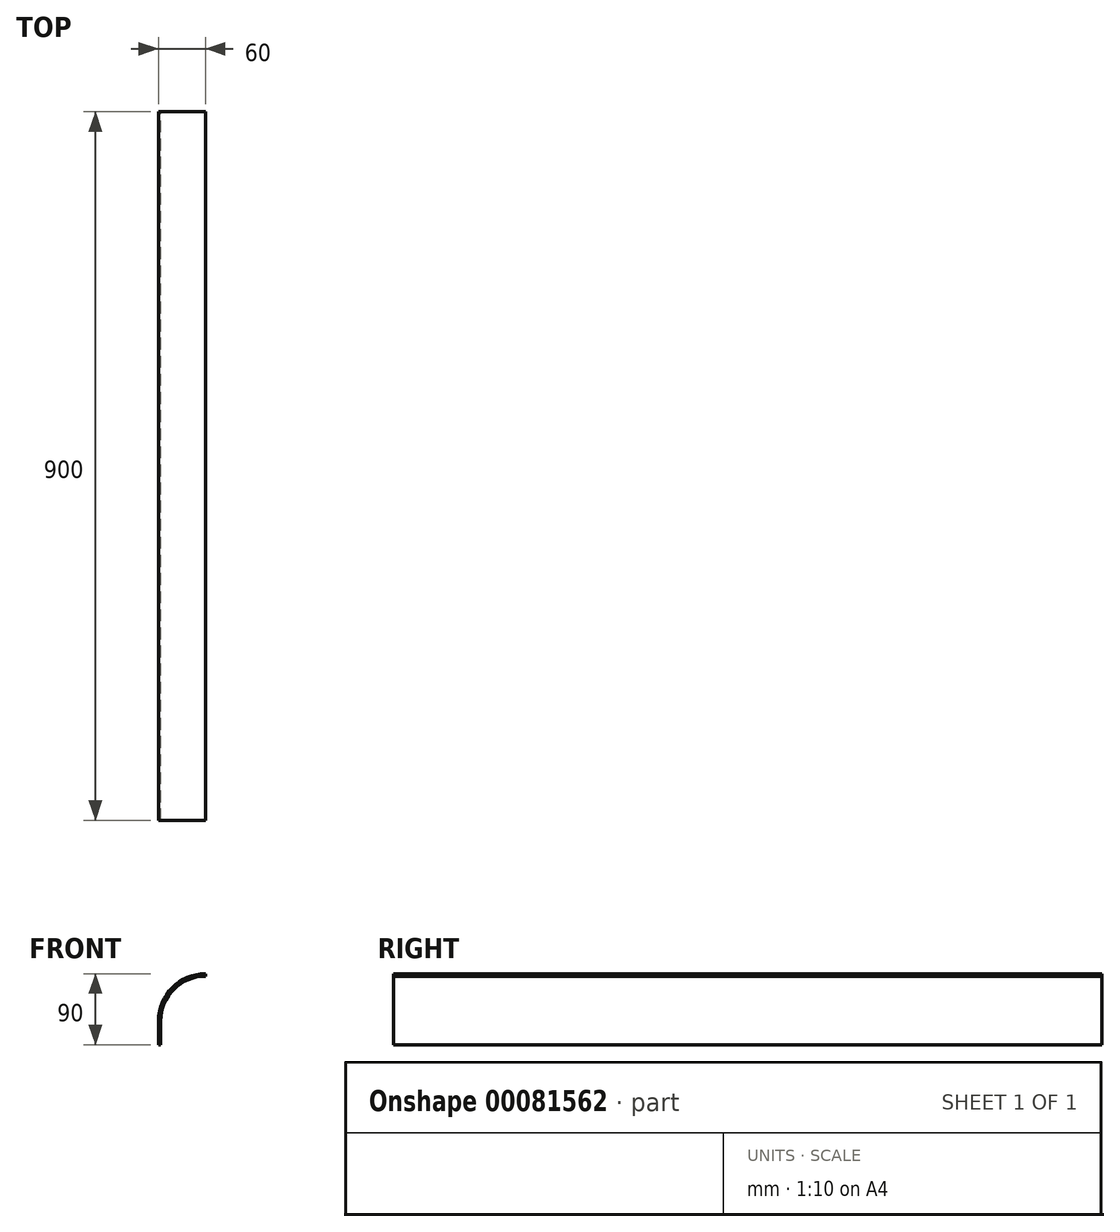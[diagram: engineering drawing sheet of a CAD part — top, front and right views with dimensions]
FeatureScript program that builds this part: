
annotation { "Feature Type Name" : "Feature", "Feature Type Description" : "" }
export const myFeature = defineFeature(function(context is Context, id is Id, definition is map)
    precondition{}
    {
        {
            var Q0;
            Q0=qCreatedBy(makeId("Front.planeOp"),FACE);
            var sketch = newSketch(context, id + "F0", { "sketchPlane" : qUnion([Q0])});
            skArc(sketch, "E0", {"start": v(-60, 0) * mm, "mid": v(-42.43, 42.43) * mm, "end": v(0, 60) * mm});
            skArc(sketch, "E1", {"start": v(-57, 0) * mm, "mid": v(-40.3, 40.3) * mm, "end": v(0, 57) * mm});
            skLineSegment(sketch, "E2", {"start": v(0, 57) * mm, "end": v(0, 60) * mm});
            skLineSegment(sketch, "E3", {"start": v(-60, 0) * mm, "end": v(-60, -30) * mm});
            skLineSegment(sketch, "E4", {"start": v(-60, -30) * mm, "end": v(-57, -30) * mm});
            skLineSegment(sketch, "E5", {"start": v(-57, -30) * mm, "end": v(-57, 0) * mm});
            skSolve(sketch);
        }
        {
            var Q0;
            Q0 = qSketchRegion(id + "F0", true);
            extrude(context, id + "F1", {"entities" : qUnion([Q0]), "depth" : 900 * mm});
        }
    });
